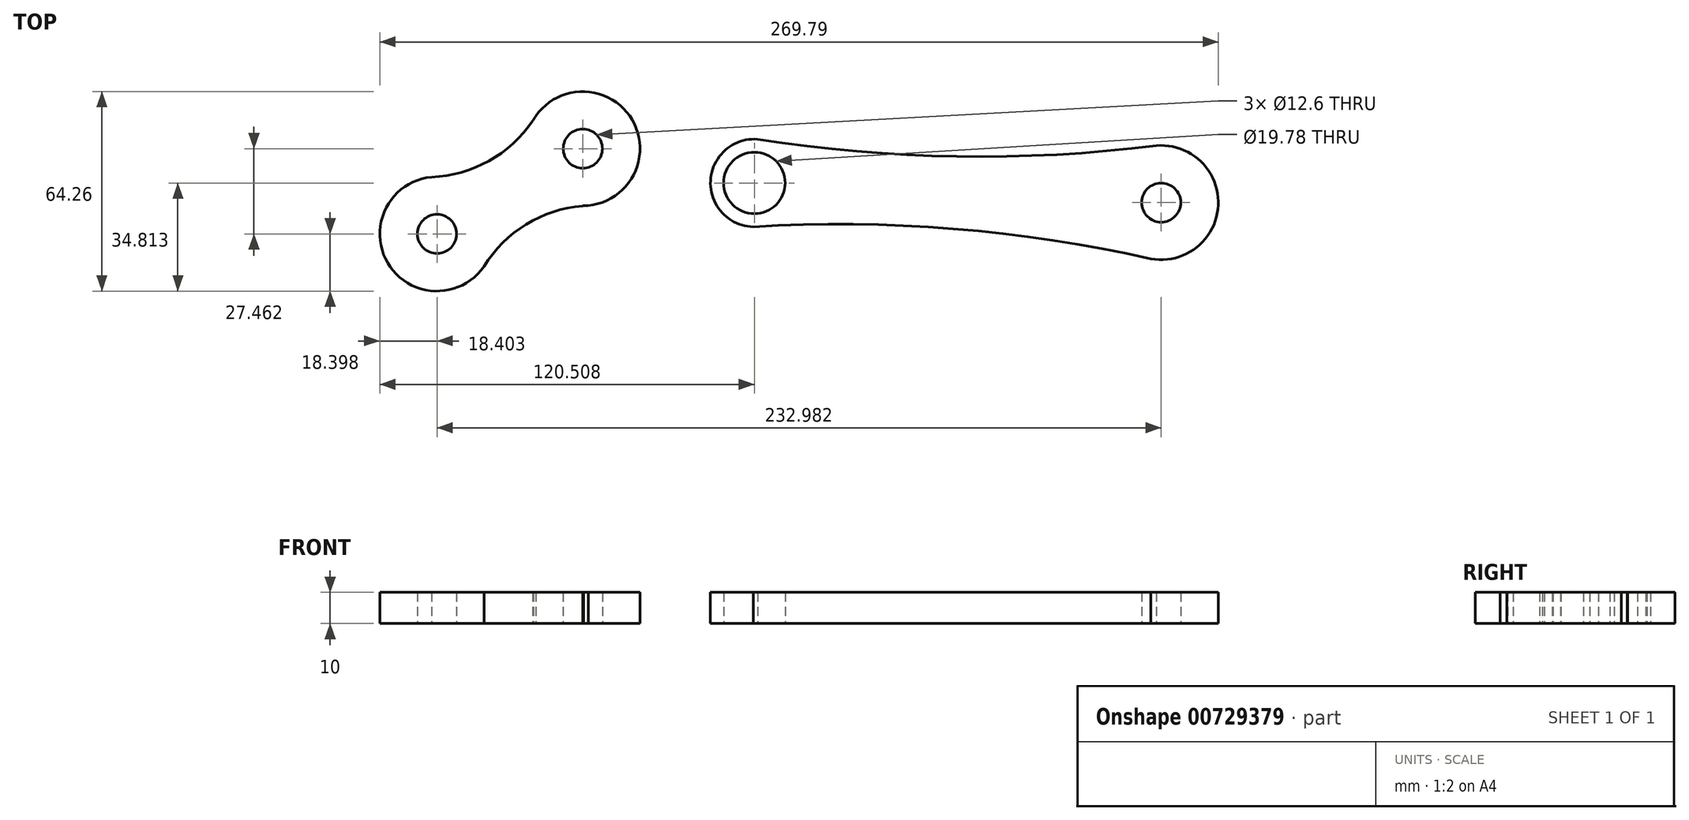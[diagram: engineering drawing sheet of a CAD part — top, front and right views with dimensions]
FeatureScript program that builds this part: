
annotation { "Feature Type Name" : "Feature", "Feature Type Description" : "" }
export const myFeature = defineFeature(function(context is Context, id is Id, definition is map)
    precondition{}
    {
        {
            var Q0;
            Q0=qCreatedBy(makeId("Top.planeOp"),FACE);
            var sketch = newSketch(context, id + "F0", { "sketchPlane" : qUnion([Q0])});
            skArc(sketch, "E0", {"start": v(0.33, -18.4) * mm, "mid": v(15.88, 9.3) * mm, "end": v(-15.88, 9.29) * mm});
            skCircle(sketch, "E1", {"center": v(0, 0) * mm, "radius": 6.3 * mm});
            skLineSegment(sketch, "E2", {"start": v(-46.9, -27.46) * mm, "end": v(0, 0) * mm, "construction": true});
            skLineSegment(sketch, "E3", {"start": v(0, 0) * mm, "end": v(-10.76, 6.12) * mm, "construction": true});
            skLineSegment(sketch, "E4", {"start": v(0, 0) * mm, "end": v(0.08, -12.54) * mm, "construction": true});
            skLineSegment(sketch, "E5", {"start": v(-23.45, -13.73) * mm, "end": v(-35.04, 6.06) * mm, "construction": true});
            skLineSegment(sketch, "E6.MirrorCS", {"start": v(-46.9, -27.46) * mm, "end": v(-36, -33.67) * mm, "construction": true});
            skLineSegment(sketch, "E7.MirrorCS", {"start": v(-46.9, -27.46) * mm, "end": v(-46.97, -15.09) * mm, "construction": true});
            skPoint(sketch, "E8.first.point", {"position": v(0.11, -18.4) * mm});
            skPoint(sketch, "E8.second.point", {"position": v(-38.9, -32.01) * mm});
            skPoint(sketch, "E8.third.point", {"position": v(81.5, -75.85) * mm});
            skPoint(sketch, "E9.third.point", {"position": v(125.08, -77.43) * mm});
            skArc(sketch, "E10.filletArc", {"start": v(0.33, -18.4) * mm, "mid": v(0.1, -18.4) * mm, "end": v(-0.12, -18.44) * mm});
            skArc(sketch, "E11.filletArc", {"start": v(-38.2, -31.63) * mm, "mid": v(-38.8, -32.05) * mm, "end": v(-39.26, -32.6) * mm});
            skPoint(sketch, "E12.visualSharp", {"position": v(-16, 9.1) * mm});
            skArc(sketch, "E12.filletArc", {"start": v(-16.14, 8.92) * mm, "mid": v(-16, 9.1) * mm, "end": v(-15.88, 9.29) * mm});
            skPoint(sketch, "E13.visualSharp", {"position": v(-46.95, -18.26) * mm});
            skArc(sketch, "E13.filletArc", {"start": v(-47.63, -18.3) * mm, "mid": v(-46.93, -18.15) * mm, "end": v(-46.28, -17.84) * mm});
            skArc(sketch, "E14.MirrorCS", {"start": v(-31.01, -36.75) * mm, "mid": v(-62.77, -36.76) * mm, "end": v(-47.22, -9.07) * mm});
            skCircle(sketch, "E15.MirrorC", {"center": v(-46.9, -27.46) * mm, "radius": 6.3 * mm});
            skArc(sketch, "E16", {"start": v(1.76, -18.32) * mm, "mid": v(-17.47, -23.94) * mm, "end": v(-31.78, -37.96) * mm});
            skPoint(sketch, "E16.third.point", {"position": v(6.44, -18.4) * mm});
            skArc(sketch, "E17.MirrorCS", {"start": v(-15.11, 10.5) * mm, "mid": v(-29.43, -3.52) * mm, "end": v(-48.66, -9.15) * mm});
            skSolve(sketch);
        }
        {
            var Q0;
            Q0=makeQuery(id+"F0.imprint","IMPRINT",FACE,{"disambiguationData":[TD([[makeQuery(id+"F0.imprint","IMPRINT",EDGE,{"derivedFrom":sQuery(id+"F0.wireOp",EDGE,"E1")}),-1.0]])]});
            extrude(context, id + "F1", {"entities" : qUnion([Q0]), "depth" : 10 * mm, "offsetDistance" : 25 * mm});
        }
        {
            var Q0;
            Q0=qCreatedBy(makeId("Top.planeOp"),FACE);
            var sketch = newSketch(context, id + "F2", { "sketchPlane" : qUnion([Q0])});
            skArc(sketch, "E18", {"start": v(58.53, 2.68) * mm, "mid": v(41.1, -10.37) * mm, "end": v(57.2, -25.03) * mm});
            skCircle(sketch, "E19", {"center": v(55.2, -11.05) * mm, "radius": 9.9 * mm});
            skArc(sketch, "E20", {"start": v(181.35, -35.14) * mm, "mid": v(204.46, -18.24) * mm, "end": v(183.08, 0.8) * mm});
            skCircle(sketch, "E21", {"center": v(186.09, -17.36) * mm, "radius": 6.3 * mm});
            skLineSegment(sketch, "E22", {"start": v(55.2, -11.05) * mm, "end": v(186.09, -17.36) * mm, "construction": true});
            skLineSegment(sketch, "E23", {"start": v(120.65, -14.2) * mm, "end": v(122.98, 34.28) * mm, "construction": true});
            skArc(sketch, "E24", {"start": v(56.22, 3.04) * mm, "mid": v(120.31, -2.54) * mm, "end": v(184.55, 0.98) * mm});
            skPoint(sketch, "E24.first.point", {"position": v(58.53, 2.68) * mm});
            skPoint(sketch, "E24.second.point", {"position": v(184.55, 0.98) * mm});
            skPoint(sketch, "E24.third.point", {"position": v(79.08, 0) * mm});
            skArc(sketch, "E25.MirrorCS", {"start": v(54.86, -25.16) * mm, "mid": v(119.2, -25.78) * mm, "end": v(182.8, -35.46) * mm});
            skSolve(sketch);
        }
        {
            var Q0;
            Q0=makeQuery(id+"F2.imprint","IMPRINT",FACE,{"disambiguationData":[TD([[makeQuery(id+"F2.imprint","IMPRINT",EDGE,{"derivedFrom":sQuery(id+"F2.wireOp",EDGE,"E19")}),-1.0]])]});
            extrude(context, id + "F3", {"entities" : qUnion([Q0]), "depth" : 10 * mm, "offsetDistance" : 25 * mm});
        }
    });
